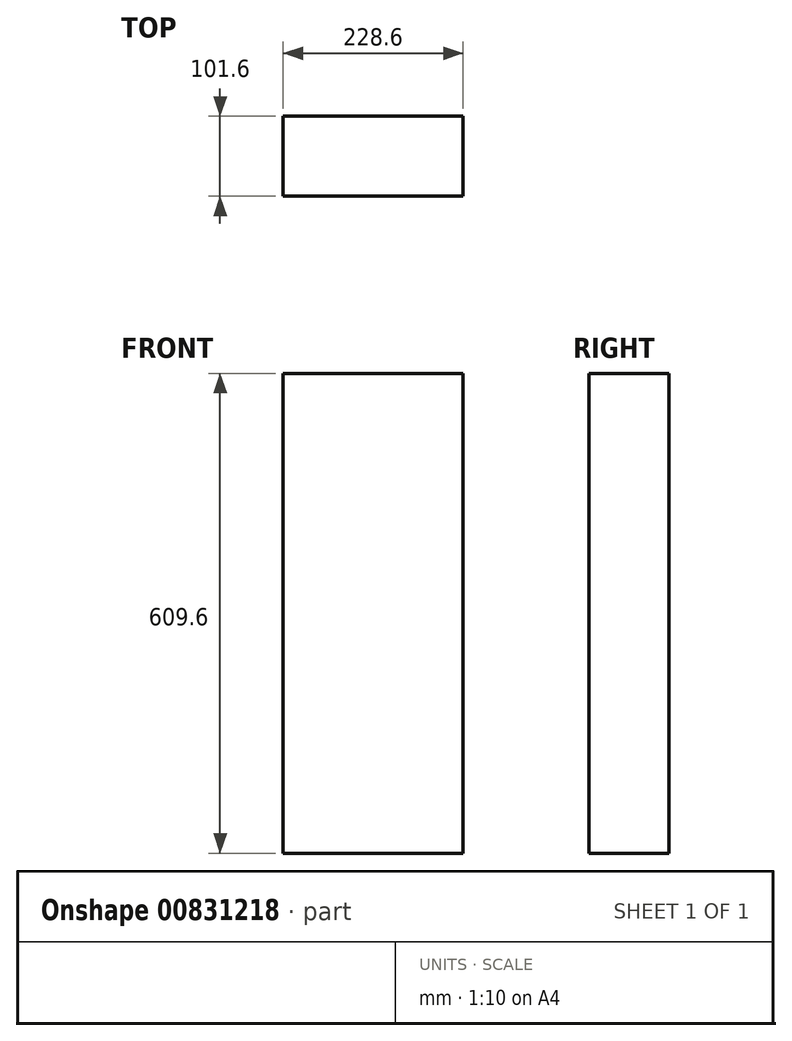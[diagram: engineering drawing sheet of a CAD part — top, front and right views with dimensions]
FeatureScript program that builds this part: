
annotation { "Feature Type Name" : "Feature", "Feature Type Description" : "" }
export const myFeature = defineFeature(function(context is Context, id is Id, definition is map)
    precondition{}
    {
        {
            var Q0;
            Q0=qCreatedBy(makeId("Front.planeOp"),FACE);
            var sketch = newSketch(context, id + "F0", { "sketchPlane" : qUnion([Q0])});
            skLineSegment(sketch, "E0.bottom", {"start": v(114.3, 304.8) * mm, "end": v(-114.3, 304.8) * mm});
            skLineSegment(sketch, "E0.top", {"start": v(114.3, -304.8) * mm, "end": v(-114.3, -304.8) * mm});
            skLineSegment(sketch, "E0.left", {"start": v(114.3, 304.8) * mm, "end": v(114.3, -304.8) * mm});
            skLineSegment(sketch, "E0.right", {"start": v(-114.3, 304.8) * mm, "end": v(-114.3, -304.8) * mm});
            skPoint(sketch, "E0.middle", {"position": v(0, 0) * mm});
            skSolve(sketch);
        }
        {
            var Q0;
            Q0=qSketchRegion(id+"F0",true);
            extrude(context, id + "F1", {"entities" : qUnion([Q0]), "depth" : 101.6 * mm, "offsetDistance" : 25.4 * mm});
        }
    });
